# Revit family: Comfort_Window_F_Side_Hung_Standard
name_source: partatom
category: Windows
revit_build: Autodesk Revit 2014 (Build: 20130308_1515(x64)
units: mm (PartAtom-declared; Revit-internal decimal feet)

## types (4) — shared parameters
DG Gasket Thickness = 12 mm  [stored 0.0393701 ft]
Description = Comfort Window, Side Hung, Type F
Double Glazing Gasket Finish = Double Glazing Gasket Material
Frame Depth = 33 mm  [stored 0.108268 ft]
Frame Edge Thickness = 26 mm
Limit Fixed Pane Height Max = 1800 mm  [stored 5.90551 ft]
Limit Fixed Pane Height Min = 200 mm  [stored 0.656168 ft]
Limit Fixed Pane Width Max = 1800 mm  [stored 5.90551 ft]
Limit Fixed Pane Width Min = 200 mm  [stored 0.656168 ft]
Limit Sash Height Max = 1200 mm
Limit Sash Height Min = 300 mm  [stored 0.984252 ft]
Limit Sash Width Max = 600 mm  [stored 1.9685 ft]
Limit Sash Width Min = 300 mm  [stored 0.984252 ft]
Limit Window Height Max = 1852 mm
Manufacturer = Crealco
Max System DG One Piece Thickness = 4 mm  [stored 0.0131234 ft]
Max System DG Unit Thickness = 20 mm  [stored 0.0656168 ft]
Model = Comfort Window
Mullion Width = 27 mm  [stored 0.0885827 ft]
Rough Height = 590 mm  [stored 1.9357 ft]
Rough Width = 902 mm  [stored 2.95932 ft]
Sash Frame Gap = 5 mm  [stored 0.0164042 ft]
Sash Frame Side Gap = 12 mm  [stored 0.0393701 ft]
Sash Side Gap = 38 mm
Set Sash Height = 1115 mm  [stored 3.65814 ft]
Set Sash Width = 515 mm  [stored 1.68963 ft]
Transom Height = 27 mm  [stored 0.0885827 ft]
URL = http://www.crealco.co.za
zero-valued in all types: Visual Light Transmittance

## per-type parameters (varying)
| type | Clearvue SHGC Value | Clearvue U Value | Energy Advantage SHGC Value | Energy Advantage U Value | Intruderprufe LowE SHGC Value | Intruderprufe LowE U Value | Intruderprufe SHGC Value | Intruderprufe U Value | SmartGlass Elite SHGC Value | SmartGlass Elite U Value | SmartGlass Plus SHGC Value | SmartGlass Plus U Value | SmartGlass Standard SHGC Value | SmartGlass Standard U Value | SmartGlass Superior SHGC Value | SmartGlass Superior U Value | Window Height | Window Width |
| Comfort-2418SS | 0.66 | 6.05 | 0.591 | 4.45 | 0.556 | 4.33 | 0.626 | 5.94 | 0.319 | 2.93 | 0.436 | 3.1 | 0.586 | 3.7 | 0.277 | 2.93 | 1790 mm  [stored 5.8727 ft] | 2390 mm  [stored 7.84121 ft] |
| Comfort-1815SS | 0.616 | 6.08 | 0.522 | 4.61 | 0.522 | 4.49 | 0.586 | 5.98 | 0.301 | 3.21 | 0.409 | 3.36 | 0.549 | 3.91 | 0.262 | 3.22 | 1490 mm  [stored 4.88845 ft] | 1790 mm  [stored 5.8727 ft] |
| Comfort-2415SS | 0.642 | 6.06 | 0.575 | 4.51 | 0.543 | 4.4 | 0.61 | 5.95 | 0.311 | 3.04 | 0.425 | 3.2 | 0.571 | 3.78 | 0.271 | 3.04 | 1490 mm  [stored 4.88845 ft] | 2390 mm  [stored 7.84121 ft] |
| Comfort-1818SS | 0.635 | 6.07 | 0.569 | 4.54 | 0.537 | 4.43 | 0.603 | 5.95 | 0.309 | 3.09 | 0.421 | 3.25 | 0.565 | 3.82 | 0.269 | 3.1 | 1790 mm  [stored 5.8727 ft] | 1790 mm  [stored 5.8727 ft] |

note: [stored X ft] marks values corroborated as IEEE doubles in the binary element streams (Revit-internal decimal feet)

## geometry (parser evidence)
native form markers: Sweep x18
no freeform markers — native parametric forms only
